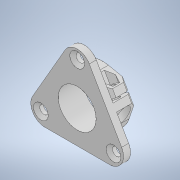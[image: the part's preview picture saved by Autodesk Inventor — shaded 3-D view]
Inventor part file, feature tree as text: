
AUTODESK INVENTOR PART (.ipt)
format: ipt  version: 2022 (Build 260153000, 153)  size: 250,880 bytes
history: native  units: mm
features: extrude x7, sketch x7, projected_geometry x3, hole x2, fillet x1, chamfer x1
ambient origin geometry x8: Origin, YZ Plane, XZ Plane, XY Plane, X Axis, Y Axis, Z Axis, Center Point
bodies: Solid1 (feature_tree)
feature tree (21):
  extrude  "Extrusion1"  Depth=4.0mm
  fillet  "Fillet1"  Radius=4.0mm
  extrude  "Extrusion2"  Depth=16.0mm
  sketch  "Sketch3"  dims[d5=6.0mm d6=3.0mm d7=0.0mm]
  extrude  "Extrusion3"  Depth=3.0mm TaperAngle=0.0deg
  extrude  "Extrusion4"  Depth=6.0mm
  sketch  "Sketch4"  dims[d8=6.0mm d9=3.8mm]
  extrude  "Extrusion5"  Depth=3.0mm
  extrude  "Extrusion6"  Depth=8.0mm TaperAngle=0.0deg
  extrude  "Extrusion7"  Depth=1.5mm
  hole  "Hole1"  [1 undecoded]
  hole  "Hole2"  [1 undecoded]
  chamfer  "Chamfer3"  Distance=6.0mm
  sketch  "Sketch1"  dims[d0=16.2mm d1=4.0mm d2=4.0mm]
  sketch  "Sketch2"  dims[d3=4.0mm d4=16.0mm]
  projected_geometry  "Projected Loop1"
  sketch  "Sketch5"  dims[d10=1.0mm d11=3.0mm]
  sketch  "Sketch6"  dims[d12=3.0mm d13=8.0mm d14=0.0mm]
  projected_geometry  "Projected Loop2"
  sketch  "Sketch7"  dims[d15=3.0mm d16=5.0mm d17=8.75mm d18=0.0mm d19=3.0mm d20=0.0mm d21=6.0mm d22=3.0mm d23=0.0mm d24=0.0mm d25=3.0mm d26=0.0mm d27=0.3mm d28=0.0mm d32=2.0mm d33=2.0mm d34=2.0mm d35=3.6mm d36=6.0mm d37=6.3mm d38=2.0mm d39=90.0deg d40=8.0mm d41=20.594885mm d45=2.9mm d46=6.0mm d47=5.5mm d48=2.0mm d49=90.0deg d50=7.0mm d51=20.594885mm d52=1.5mm d53=2.0mm d54=45.0deg]
  projected_geometry  "Projected Loop3"
note: 2 required parameter values undecoded (feature->parameter linkage not recoverable at this tier; creation-order binding heuristic only, values carry confidence <= 0.55)
